# Revit family: Connection-Welded Shear Stud-Composite Floor Decking
name_source: partatom
category: Structural Connections
revit_build: Autodesk Revit 2017 (Build: 20170118_1100(x64)
units: mm (PartAtom-declared; Revit-internal decimal feet)

## family parameters
Cut with Voids When Loaded = No
Enable cutting in views = Yes
Host = Face
Material for Model Behavior = Steel
Shared = No

## types (11) — shared parameters
CBICode = 3151
CBIDescription = Composite construction of in situ concrete and permanent formwork
ComFlor Design Software = http://www.comflor.nz
ComFlor Technical Resources = http://www.comflor.nz
Default Elevation = 1219 mm
Description = Stud shear connector for use with ComFlor® range
Head = 12 mm  [stored 0.0393701 ft]
Head Radius = 16 mm  [stored 0.0524934 ft]
Manufacturer = Supplied by Steel & Tube
ManufacturerName = Supplied by Steel & Tube
ManufacturerURL = http://www.steelandtube.co.nz
Material Standard = AS/NZS 1554.2:2003
Model = Welded Shear Stud
SpecificationDescription = ComFlor composite floor system
SpecificationReference = 3151C
Stud Material = Metal
Stud Radius = 10 mm  [stored 0.0328084 ft]
Trademark = ComFlor® is a registered trade mark used in Australia and New Zealand under licence from Tata Steel UK Limited.
Type Comments = G450 Steel
URL = http://www.comflor.nz
Uniclass2015Code = Ss_30_12_85_16
Uniclass2015Title = Composite steel and concrete floor, roof or balcony deck systems
Uniclass2015Version = 2015

## per-type parameters (varying)
| type | Stud Length |
| 50mm | 50 mm |
| 75mm | 75 mm |
| 100mm | 100 mm  [stored 0.328084 ft] |
| 125mm | 125 mm |
| 150mm | 150 mm |
| 175mm | 175 mm |
| 200mm | 200 mm |
| 225mm | 225 mm |
| 250mm | 250 mm |
| 275mm | 275 mm |
| 300mm | 300 mm |

note: [stored X ft] marks values corroborated as IEEE doubles in the binary element streams (Revit-internal decimal feet)

## geometry (parser evidence)
native form markers: Sweep x1
no freeform markers — native parametric forms only
